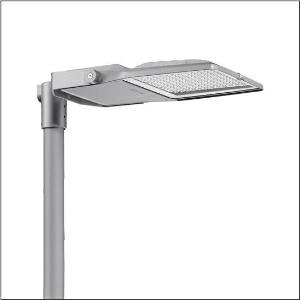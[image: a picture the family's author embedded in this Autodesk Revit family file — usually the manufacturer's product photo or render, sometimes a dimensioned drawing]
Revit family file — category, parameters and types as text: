
# Revit family: floodlight_fl_21_midi___pl33t_5xa7786f2f3a_5712
name_source: partatom
category: Lighting Fixtures
units: mm (PartAtom-declared; Revit-internal decimal feet)

## family parameters
Cut with Voids When Loaded = No
Host = Face
Light Source = No
Part Type = Normal
Room Calculation Point = No
Round Connector Dimension = Use Diameter
Shared = No

## types (1)
- --- (1 x LED, 35340 lm, 271.6 W, 3000K)
    Apparent Load = 272 VA
    CIE Flux Codes = 26 75 99 100 100
    Color Rendering = 70
    Color Temperature = 3000K
    Default Elevation = 1800 mm
    Description = Floodlight FL 21 midi, floodlight, primary light control with lens, of PMMA, primary optical cover: protective disc, of toughened safety glass, transparent, light distribution: PL33T, light emission: direct distribution, installation type: surface-mounted, LED, High Power LED, rated luminous flux: 35.340lm, luminous efficacy: 130lm/W, light colour: 730, colour temperature: 3000K, control gear: ECG Smart Interface, control: flexible luminous flux parameterisation, time-dependent luminous flux control, constant luminous flux control, overheat protection, presetting dimming logarithmic, with terminal, 6-pole, mains connection: 220..240V, AC, 50/60Hz, start of lifetime: 272W, end of service life: 287W, reduction: 123W, luminaire housing, of diecast aluminium, powder-coated, Siteco® metallic grey (DB 702S), corrosivity category C5 mid according to DIN EN ISO 12944, sealing non-destructively replaceable, please order mast flange separately, mast bracket, of steel, galvanised, powder-coated, Siteco® metallic grey (DB 702S), Smart Interface below and above, protection rating (complete): IP66, insulation class (complete): insulation class II (safety insulation), certification: CE, protection symbol: D, impact resistance: IK08, permissible operating ambient temperature: -40..+40°C, permissible operating ambient temperature for outdoor applications: -40..+50°C, standard: DIN EN 12944, LABS conformity tested according to VDMA 24364:2018-05, packaging unit: 1 piece

Light Distribution: PL33T
    Height = 76 mm
    Lamp = 1 x LED
    Lamp Light Flux = 35340 lm
    Lamp Power = 271.6 W
    Lamp count = 1
    Length = 657 mm
    Luminous efficacy = 130 lm/W
    Manufacturer = Siteco
    ModVariant = No
    Model = 5XA7786F2F3A
    Number of Poles = 1
    OnlyDefault = Yes
    Power Factor = 1
    Product Name = Floodlight FL 21 midi | PL33T
    Product group = floodlight | pylon annexe
    ProductGroupID = 6200
    Protection Class = Protection class II
    Protection Degree = IP 66
    RLX_Detail_Level = 1
    RLX_Emergency_Light_Flux = 0 lm
    RLX_Emergency_Type = 0
    RLX_Emergency_Type_DB = No
    RlxData = <blob elided: 153557 chars, md5=e1b97eed>
    Socket = socket
    Standby Power = 0 W
    System Light Flux = 35340 lm
    System Power = 272 W
    Type Comments = factory setting: luminous flux: 100 % | dim-lin: 254 | 620 mA
    Type Image = l_1007123.jpg
    URL = http://relux.com
    VarID = @adj_100549
    Voltage = 0 V
    Weight = 0.00 kg
    Width = 442 mm

## geometry (parser evidence)
native form markers: Blend x4, Sweep x13
no freeform markers — native parametric forms only
